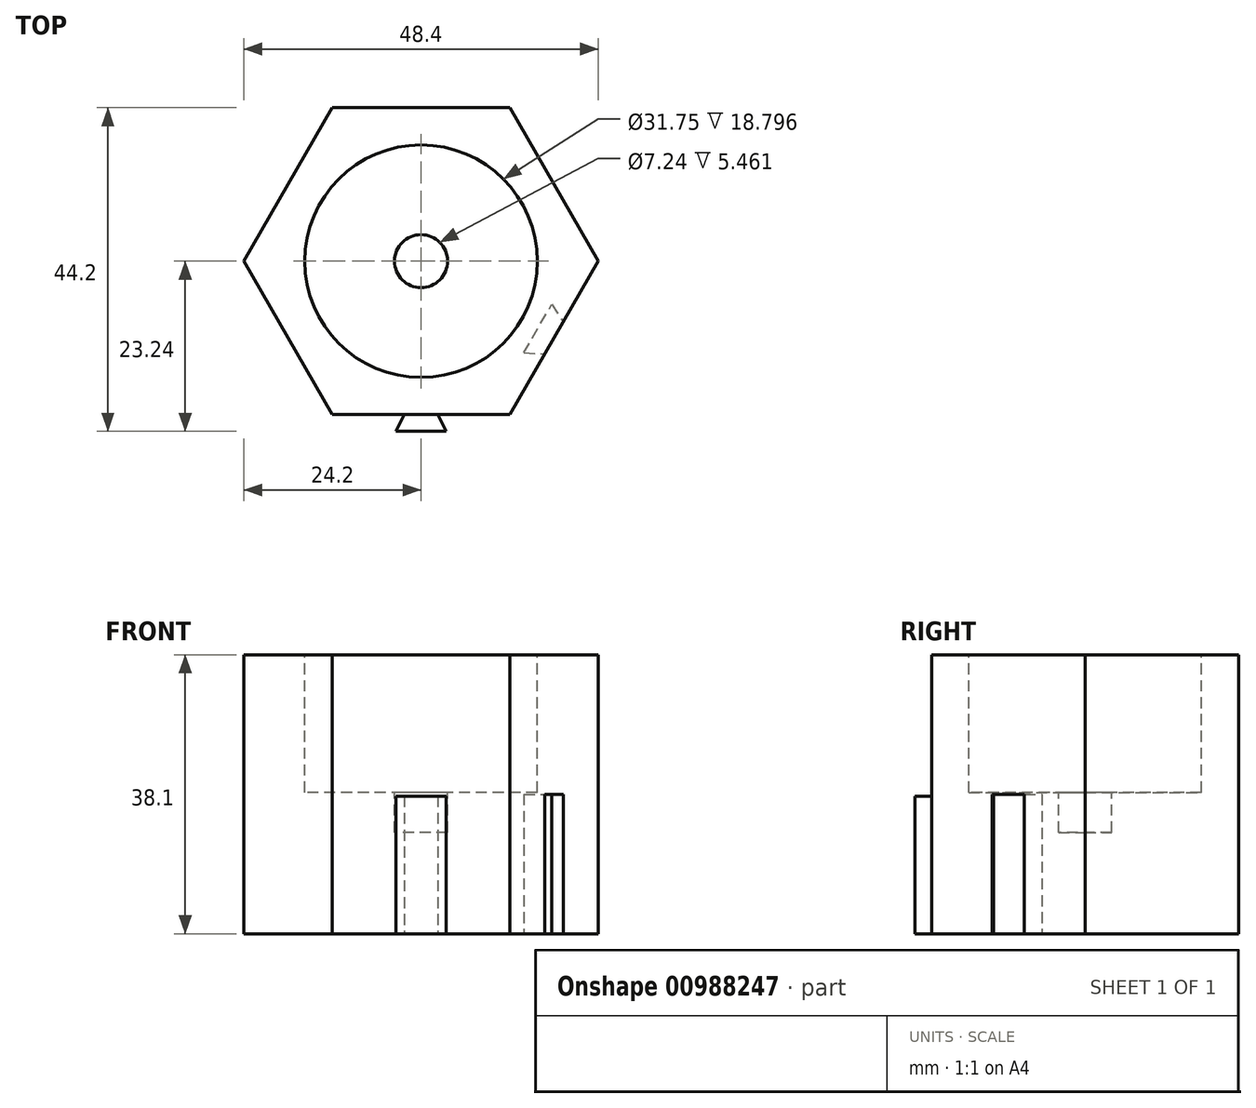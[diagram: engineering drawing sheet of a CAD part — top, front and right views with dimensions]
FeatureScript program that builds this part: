
annotation { "Feature Type Name" : "Feature", "Feature Type Description" : "" }
export const myFeature = defineFeature(function(context is Context, id is Id, definition is map)
    precondition{}
    {
        {
            var Q0;
            Q0=qCreatedBy(makeId("Top.planeOp"),FACE);
            var sketch = newSketch(context, id + "F0", { "sketchPlane" : qUnion([Q0])});
            skCircle(sketch, "E0.cCircle", {"center": v(0, 0) * mm, "radius": 20.96 * mm, "construction": true});
            skLineSegment(sketch, "E0.0", {"start": v(12.1, -20.96) * mm, "end": v(-12.1, -20.96) * mm});
            skLineSegment(sketch, "E0.1", {"start": v(-12.1, -20.96) * mm, "end": v(-24.2, 0) * mm});
            skLineSegment(sketch, "E0.2", {"start": v(-24.2, 0) * mm, "end": v(-12.1, 20.95) * mm});
            skLineSegment(sketch, "E0.3", {"start": v(-12.1, 20.95) * mm, "end": v(12.1, 20.96) * mm});
            skLineSegment(sketch, "E0.4", {"start": v(12.1, 20.96) * mm, "end": v(24.2, 0) * mm});
            skLineSegment(sketch, "E0.5", {"start": v(24.2, 0) * mm, "end": v(12.1, -20.96) * mm});
            skPoint(sketch, "E0.0.midPoint", {"position": v(0, -20.96) * mm});
            skSolve(sketch);
        }
        {
            var Q0;
            Q0 = qSketchRegion(id + "F0", true);
            extrude(context, id + "F1", {"entities" : qUnion([Q0]), "depth" : 38.1 * mm, "offsetDistance" : 25.4 * mm});
        }
        {
            var Q0;
            Q0=makeQuery(id+"F1.opExtrude","CAP_FACE",FACE,{"disambiguationData":[OSD([sQuery(id+"F0.wireOp",EDGE,"E0.0"),sQuery(id+"F0.wireOp",EDGE,"E0.1"),sQuery(id+"F0.wireOp",EDGE,"E0.2"),sQuery(id+"F0.wireOp",EDGE,"E0.3"),sQuery(id+"F0.wireOp",EDGE,"E0.4"),sQuery(id+"F0.wireOp",EDGE,"E0.5")])],"isStart":false});
            var sketch = newSketch(context, id + "F2", { "sketchPlane" : qUnion([Q0])});
            skCircle(sketch, "E1.cCircle", {"center": v(0, 0) * mm, "radius": 19.68 * mm, "construction": true});
            skLineSegment(sketch, "E1.0", {"start": v(11.37, -19.68) * mm, "end": v(-11.37, -19.68) * mm});
            skLineSegment(sketch, "E1.1", {"start": v(-11.37, -19.68) * mm, "end": v(-22.73, 0) * mm});
            skLineSegment(sketch, "E1.2", {"start": v(-22.73, 0) * mm, "end": v(-11.37, 19.68) * mm});
            skLineSegment(sketch, "E1.3", {"start": v(-11.37, 19.68) * mm, "end": v(11.37, 19.69) * mm});
            skLineSegment(sketch, "E1.4", {"start": v(11.37, 19.69) * mm, "end": v(22.73, 0) * mm});
            skLineSegment(sketch, "E1.5", {"start": v(22.73, 0) * mm, "end": v(11.37, -19.68) * mm});
            skPoint(sketch, "E1.0.midPoint", {"position": v(0, -19.68) * mm});
            skSolve(sketch);
        }
        {
            var Q0;
            Q0 = qSketchRegion(id + "F2", true);
            extrude(context, id + "F3", {"entities" : qUnion([Q0]), "operationType" : NewBodyOperationType.REMOVE, "oppositeDirection" : true, "depth" : 18.8 * mm, "offsetDistance" : 25.4 * mm});
        }
        {
            var Q0;
            Q0=makeQuery(id+"F1.opExtrude","CAP_FACE",FACE,{"disambiguationData":[OSD([sQuery(id+"F0.wireOp",EDGE,"E0.0"),sQuery(id+"F0.wireOp",EDGE,"E0.1"),sQuery(id+"F0.wireOp",EDGE,"E0.2"),sQuery(id+"F0.wireOp",EDGE,"E0.3"),sQuery(id+"F0.wireOp",EDGE,"E0.4"),sQuery(id+"F0.wireOp",EDGE,"E0.5")])],"isStart":false});
            var sketch = newSketch(context, id + "F4", { "sketchPlane" : qUnion([Q0])});
            skCircle(sketch, "E2", {"center": v(0, 0) * mm, "radius": 15.88 * mm});
            skSolve(sketch);
        }
        {
            var Q0;
            Q0=makeQuery(id+"F4.imprint","IMPRINT",FACE,{"disambiguationData":[TD([[makeQuery(id+"F4.imprint","IMPRINT",EDGE,{"derivedFrom":sQuery(id+"F4.wireOp",EDGE,"E2")}),-1.0]])]});
            extrude(context, id + "F5", {"entities" : qUnion([Q0]), "operationType" : NewBodyOperationType.ADD, "oppositeDirection" : true, "depth" : 18.8 * mm, "offsetDistance" : 25.4 * mm});
        }
        {
            var Q0;
            Q0=makeQuery(id+"F5.boolean.opBoolean","MERGE",FACE,{"derivedFrom":[makeQuery(id+"F1.opExtrude","CAP_FACE",FACE,{"disambiguationData":[OSD([sQuery(id+"F0.wireOp",EDGE,"E0.0"),sQuery(id+"F0.wireOp",EDGE,"E0.1"),sQuery(id+"F0.wireOp",EDGE,"E0.2"),sQuery(id+"F0.wireOp",EDGE,"E0.3"),sQuery(id+"F0.wireOp",EDGE,"E0.4"),sQuery(id+"F0.wireOp",EDGE,"E0.5")])],"isStart":false}),makeQuery(id+"F5.opExtrude","CAP_FACE",FACE,{"disambiguationData":[OSD([sQuery(id+"F2.wireOp",EDGE,"E1.0"),sQuery(id+"F2.wireOp",EDGE,"E1.1"),sQuery(id+"F2.wireOp",EDGE,"E1.2"),sQuery(id+"F2.wireOp",EDGE,"E1.3"),sQuery(id+"F2.wireOp",EDGE,"E1.4"),sQuery(id+"F2.wireOp",EDGE,"E1.5"),sQuery(id+"F4.wireOp",EDGE,"E2")])],"isStart":true})]});
            var sketch = newSketch(context, id + "F6", { "sketchPlane" : qUnion([Q0])});
            skCircle(sketch, "E3", {"center": v(0, 0) * mm, "radius": 3.62 * mm});
            skSolve(sketch);
        }
        {
            var Q0;
            Q0=makeQuery(id+"F6.imprint","IMPRINT",FACE,{"disambiguationData":[TD([[makeQuery(id+"F6.imprint","IMPRINT",EDGE,{"derivedFrom":sQuery(id+"F6.wireOp",EDGE,"E3")}),1.0]])]});
            extrude(context, id + "F7", {"entities" : qUnion([Q0]), "operationType" : NewBodyOperationType.REMOVE, "oppositeDirection" : true, "depth" : 24.26 * mm, "offsetDistance" : 25.4 * mm});
        }
        {
            var Q0;
            Q0=makeQuery(id+"F1.opExtrude","CAP_FACE",FACE,{"disambiguationData":[OSD([sQuery(id+"F0.wireOp",EDGE,"E0.0"),sQuery(id+"F0.wireOp",EDGE,"E0.1"),sQuery(id+"F0.wireOp",EDGE,"E0.2"),sQuery(id+"F0.wireOp",EDGE,"E0.3"),sQuery(id+"F0.wireOp",EDGE,"E0.4"),sQuery(id+"F0.wireOp",EDGE,"E0.5")])],"isStart":true});
            var sketch = newSketch(context, id + "F8", { "sketchPlane" : qUnion([Q0])});
            skLineSegment(sketch, "E4", {"start": v(0, 20.96) * mm, "end": v(0, -20.96) * mm});
            skLineSegment(sketch, "E5", {"start": v(0, 20.96) * mm, "end": v(0, 23.24) * mm});
            skLineSegment(sketch, "E6", {"start": v(0, 20.96) * mm, "end": v(-2.29, 20.96) * mm});
            skLineSegment(sketch, "E7", {"start": v(0, 23.24) * mm, "end": v(-3.43, 23.24) * mm});
            skLineSegment(sketch, "E8", {"start": v(-3.43, 23.24) * mm, "end": v(-2.29, 20.96) * mm});
            skLineSegment(sketch, "E9.MirrorCS", {"start": v(3.43, 23.24) * mm, "end": v(2.29, 20.96) * mm});
            skLineSegment(sketch, "E10.MirrorCS", {"start": v(0, 23.24) * mm, "end": v(3.43, 23.24) * mm});
            skLineSegment(sketch, "E11.MirrorCS", {"start": v(0, 20.96) * mm, "end": v(2.29, 20.96) * mm});
            skSolve(sketch);
        }
        {
            var Q0;
            Q0 = qSketchRegion(id + "F8", true);
            extrude(context, id + "F9", {"entities" : qUnion([Q0]), "operationType" : NewBodyOperationType.ADD, "oppositeDirection" : true, "depth" : 18.8 * mm, "offsetDistance" : 25.4 * mm});
        }
        {
            var Q0;
            Q0=makeQuery(id+"F9.boolean.opBoolean","MERGE",FACE,{"derivedFrom":[makeQuery(id+"F1.opExtrude","CAP_FACE",FACE,{"disambiguationData":[OSD([sQuery(id+"F0.wireOp",EDGE,"E0.0"),sQuery(id+"F0.wireOp",EDGE,"E0.1"),sQuery(id+"F0.wireOp",EDGE,"E0.2"),sQuery(id+"F0.wireOp",EDGE,"E0.3"),sQuery(id+"F0.wireOp",EDGE,"E0.4"),sQuery(id+"F0.wireOp",EDGE,"E0.5")])],"isStart":true}),makeQuery(id+"F9.opExtrude","CAP_FACE",FACE,{"disambiguationData":[OSD([sQuery(id+"F8.wireOp",EDGE,"E6"),sQuery(id+"F8.wireOp",EDGE,"E7"),sQuery(id+"F8.wireOp",EDGE,"E8"),sQuery(id+"F8.wireOp",EDGE,"E9.MirrorCS"),sQuery(id+"F8.wireOp",EDGE,"E10.MirrorCS"),sQuery(id+"F8.wireOp",EDGE,"E11.MirrorCS")])],"isStart":true})]});
            var sketch = newSketch(context, id + "F10", { "sketchPlane" : qUnion([Q0])});
            skLineSegment(sketch, "E12", {"start": v(18.15, 10.48) * mm, "end": v(-18.15, -10.48) * mm});
            skLineSegment(sketch, "E13", {"start": v(18.15, 10.48) * mm, "end": v(15.95, 9.2) * mm});
            skLineSegment(sketch, "E14", {"start": v(18.15, 10.48) * mm, "end": v(19.42, 8.28) * mm});
            skLineSegment(sketch, "E15", {"start": v(15.95, 9.2) * mm, "end": v(17.85, 5.9) * mm});
            skLineSegment(sketch, "E16", {"start": v(17.85, 5.9) * mm, "end": v(19.42, 8.28) * mm});
            skLineSegment(sketch, "E17.MirrorCS", {"start": v(15.95, 9.2) * mm, "end": v(14.04, 12.5) * mm});
            skLineSegment(sketch, "E18.MirrorCS", {"start": v(14.04, 12.5) * mm, "end": v(16.88, 12.68) * mm});
            skLineSegment(sketch, "E19.MirrorCS", {"start": v(18.15, 10.48) * mm, "end": v(16.88, 12.68) * mm});
            skSolve(sketch);
        }
        {
            var Q0;
            {var subQ0=sQuery(id+"F10.wireOp",EDGE,"E17.MirrorCS");var subQ4=sQuery(id+"F10.wireOp",EDGE,"E14");Q0=qUnion([makeQuery(id+"F10.imprint","IMPRINT",FACE,{"disambiguationData":[TD([[makeQuery(id+"F10.imprint","IMPRINT",EDGE,{"derivedFrom":subQ4}),1.0]])]}),makeQuery(id+"F10.imprint","IMPRINT",FACE,{"disambiguationData":[TD([[makeQuery(id+"F10.imprint","IMPRINT",EDGE,{"derivedFrom":subQ0}),-1.0]])]})]);}
            extrude(context, id + "F11", {"entities" : qUnion([Q0]), "operationType" : NewBodyOperationType.REMOVE, "oppositeDirection" : true, "depth" : 19.05 * mm, "offsetDistance" : 25.4 * mm});
        }
    });
